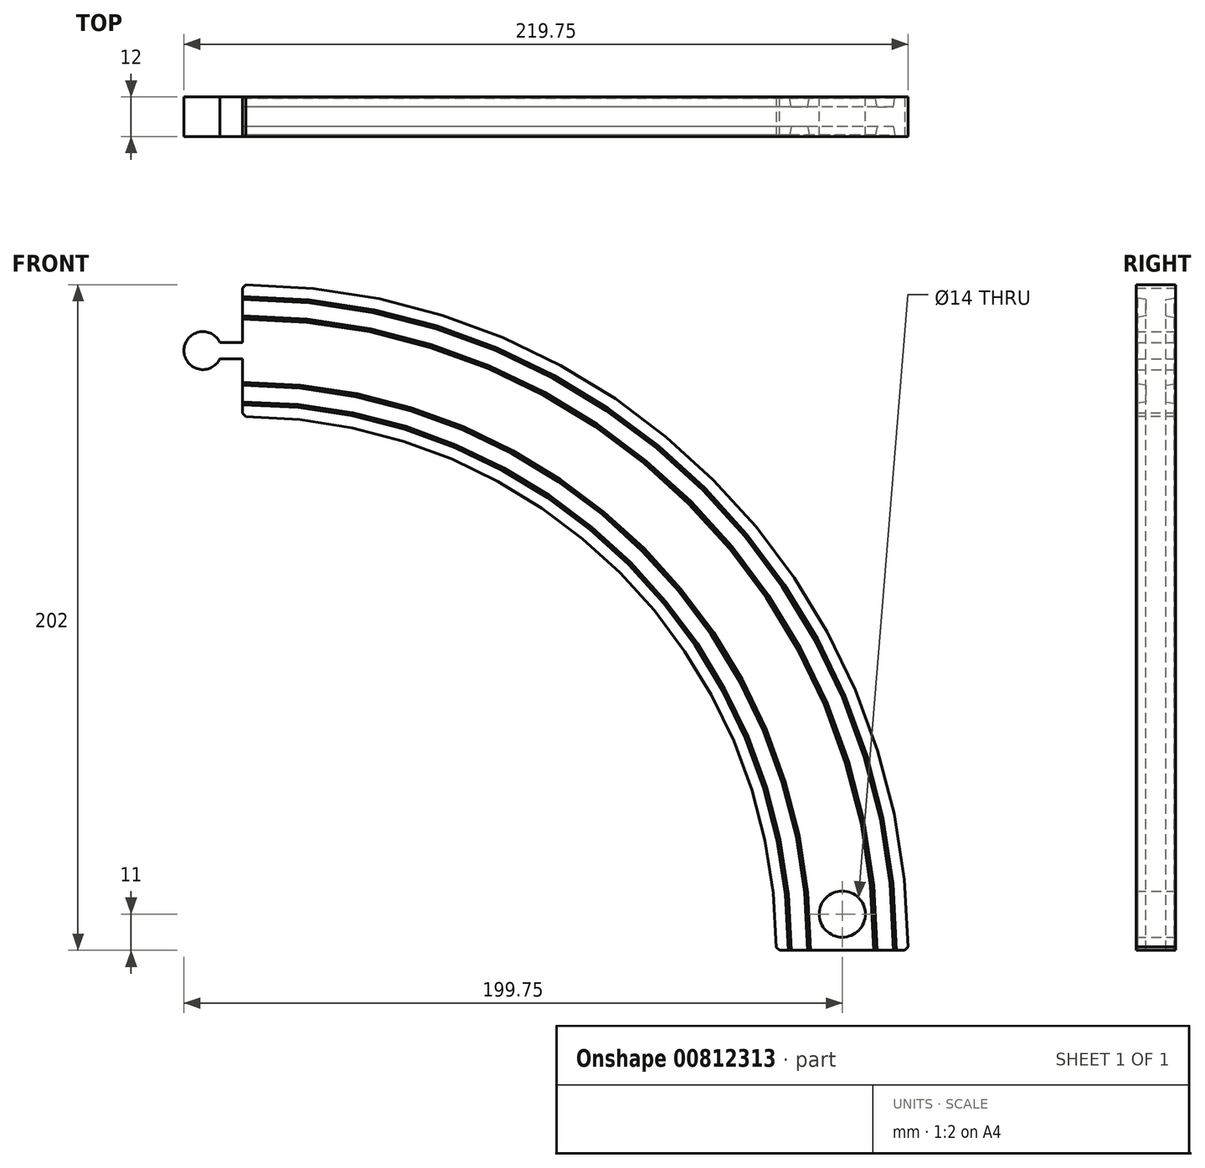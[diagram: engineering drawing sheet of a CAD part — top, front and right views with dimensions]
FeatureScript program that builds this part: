
annotation { "Feature Type Name" : "Feature", "Feature Type Description" : "" }
export const myFeature = defineFeature(function(context is Context, id is Id, definition is map)
    precondition{}
    {
        {
            var Q0;
            Q0=qCreatedBy(makeId("Top.planeOp"),FACE);
            var sketch = newSketch(context, id + "F0", { "sketchPlane" : qUnion([Q0])});
            skLineSegment(sketch, "E0.bottom", {"start": v(-20, 6) * mm, "end": v(20, 6) * mm});
            skLineSegment(sketch, "E0.top", {"start": v(-20, -6) * mm, "end": v(20, -6) * mm});
            skLineSegment(sketch, "E0.left", {"start": v(-20, 6) * mm, "end": v(-20, -6) * mm});
            skLineSegment(sketch, "E0.right", {"start": v(20, 6) * mm, "end": v(20, -6) * mm});
            skLineSegment(sketch, "E1", {"start": v(10.53, 3) * mm, "end": v(15.53, 3) * mm});
            skLineSegment(sketch, "E2", {"start": v(-15.53, 3) * mm, "end": v(-10.53, 3) * mm});
            skLineSegment(sketch, "E3", {"start": v(-20, 6) * mm, "end": v(20, -6) * mm, "construction": true});
            skLineSegment(sketch, "E4", {"start": v(-10.53, 3) * mm, "end": v(-10, 6) * mm});
            skLineSegment(sketch, "E5", {"start": v(-15.53, 3) * mm, "end": v(-16, 6) * mm});
            skLineSegment(sketch, "E6", {"start": v(10.53, 3) * mm, "end": v(10, 6) * mm});
            skLineSegment(sketch, "E7", {"start": v(15.53, 3) * mm, "end": v(16, 6) * mm});
            skLineSegment(sketch, "E8", {"start": v(15.53, -3) * mm, "end": v(10.53, -3) * mm});
            skLineSegment(sketch, "E9", {"start": v(15.53, -3) * mm, "end": v(16, -6) * mm});
            skLineSegment(sketch, "E10", {"start": v(10.53, -3) * mm, "end": v(10, -6) * mm});
            skLineSegment(sketch, "E11", {"start": v(-10.53, -3) * mm, "end": v(-15.53, -3) * mm});
            skLineSegment(sketch, "E12", {"start": v(-10.53, -3) * mm, "end": v(-10, -6) * mm});
            skLineSegment(sketch, "E13", {"start": v(-15.53, -3) * mm, "end": v(-16, -6) * mm});
            skLineSegment(sketch, "E14", {"start": v(10, 6) * mm, "end": v(10, -6) * mm, "construction": true});
            skLineSegment(sketch, "E15", {"start": v(16, 6) * mm, "end": v(16, -6) * mm, "construction": true});
            skLineSegment(sketch, "E16", {"start": v(10.53, 3) * mm, "end": v(10.53, -6) * mm, "construction": true});
            skLineSegment(sketch, "E17", {"start": v(-15.53, 3) * mm, "end": v(-15.53, -6) * mm, "construction": true});
            skSolve(sketch);
        }
        {
            var Q0;
            Q0=qCreatedBy(makeId("Front.planeOp"),FACE);
            var sketch = newSketch(context, id + "F1", { "sketchPlane" : qUnion([Q0])});
            skArc(sketch, "E18", {"start": v(0, 0) * mm, "mid": v(-53.3, 128.7) * mm, "end": v(-182, 182) * mm});
            skLineSegment(sketch, "E19", {"start": v(-182, 0) * mm, "end": v(-182, 247.89) * mm, "construction": true});
            skSolve(sketch);
        }
        {
            var Q0;
            Q0=makeQuery(id+"F0.imprint","IMPRINT",FACE,{"disambiguationData":[TD([[makeQuery(id+"F0.imprint","IMPRINT",EDGE,{"derivedFrom":sQuery(id+"F0.wireOp",EDGE,"E0.top")}),1.0]])]});
            var Q1;
            Q1=sQuery(id+"F1.wireOp",EDGE,"E18");
            sweep(context, id + "F2", {"profiles" : qUnion([Q0]), "path" : qUnion([Q1])});
        }
        {
            var Q0;
            Q0=makeQuery(id+"F2.opSweep","SWEPT_EDGE",EDGE,{"disambiguationData":[OSD([sQuery(id+"F0.wireOp",EDGE,"E0.bottom"),sQuery(id+"F0.wireOp",EDGE,"E4"),sQuery(id+"F1.wireOp",EDGE,"QheDVgyy-v1Xf-DTUT-CkoZ-R19I37jAeaWV")])]});
            var Q1;
            Q1=makeQuery(id+"F2.opSweep","SWEPT_EDGE",EDGE,{"disambiguationData":[OSD([sQuery(id+"F0.wireOp",EDGE,"E0.bottom"),sQuery(id+"F0.wireOp",EDGE,"E5"),sQuery(id+"F1.wireOp",EDGE,"QheDVgyy-v1Xf-DTUT-CkoZ-R19I37jAeaWV")])]});
            var Q2;
            Q2=makeQuery(id+"F2.opSweep","SWEPT_EDGE",EDGE,{"disambiguationData":[OSD([sQuery(id+"F0.wireOp",EDGE,"E0.bottom"),sQuery(id+"F0.wireOp",EDGE,"E6"),sQuery(id+"F1.wireOp",EDGE,"QheDVgyy-v1Xf-DTUT-CkoZ-R19I37jAeaWV")])]});
            var Q3;
            Q3=makeQuery(id+"F2.opSweep","SWEPT_EDGE",EDGE,{"disambiguationData":[OSD([sQuery(id+"F0.wireOp",EDGE,"E0.bottom"),sQuery(id+"F0.wireOp",EDGE,"E7"),sQuery(id+"F1.wireOp",EDGE,"QheDVgyy-v1Xf-DTUT-CkoZ-R19I37jAeaWV")])]});
            var Q4;
            Q4=makeQuery(id+"F2.opSweep","SWEPT_EDGE",EDGE,{"disambiguationData":[OSD([sQuery(id+"F0.wireOp",EDGE,"E0.top"),sQuery(id+"F0.wireOp",EDGE,"E10"),sQuery(id+"F1.wireOp",EDGE,"E18")])]});
            var Q5;
            Q5=makeQuery(id+"F2.opSweep","SWEPT_EDGE",EDGE,{"disambiguationData":[OSD([sQuery(id+"F0.wireOp",EDGE,"E0.top"),sQuery(id+"F0.wireOp",EDGE,"E9"),sQuery(id+"F1.wireOp",EDGE,"E18")])]});
            var Q6;
            Q6=makeQuery(id+"F2.opSweep","SWEPT_EDGE",EDGE,{"disambiguationData":[OSD([sQuery(id+"F0.wireOp",EDGE,"E0.top"),sQuery(id+"F0.wireOp",EDGE,"E13"),sQuery(id+"F1.wireOp",EDGE,"E18")])]});
            var Q7;
            Q7=makeQuery(id+"F2.opSweep","SWEPT_EDGE",EDGE,{"disambiguationData":[OSD([sQuery(id+"F0.wireOp",EDGE,"E0.top"),sQuery(id+"F0.wireOp",EDGE,"E12"),sQuery(id+"F1.wireOp",EDGE,"E18")])]});
            chamfer(context, id + "F3", {"entities" : qUnion([Q0, Q1, Q2, Q3, Q4, Q5, Q6, Q7]), "width" : 0.5 * mm, "tangentPropagation" : true});
        }
        {
            var Q0;
            Q0=qCreatedBy(makeId("Front.planeOp"),FACE);
            var sketch = newSketch(context, id + "F4", { "sketchPlane" : qUnion([Q0])});
            skLineSegment(sketch, "E20.0", {"start": v(-182, 191.5) * mm, "end": v(-182, 172.5) * mm});
            skSolve(sketch);
        }
        {
            var Q0;
            Q0=qCreatedBy(makeId("Front.planeOp"),FACE);
            var sketch = newSketch(context, id + "F5", { "sketchPlane" : qUnion([Q0])});
            skLineSegment(sketch, "E21.0", {"start": v(9.5, 0) * mm, "end": v(-9.5, 0) * mm});
            skLineSegment(sketch, "E22.bottom", {"start": v(3.5, 0) * mm, "end": v(-3.5, 0) * mm});
            skLineSegment(sketch, "E22.top", {"start": v(3.5, 5) * mm, "end": v(-3.5, 5) * mm});
            skLineSegment(sketch, "E22.left", {"start": v(3.5, 0) * mm, "end": v(3.5, 5) * mm});
            skLineSegment(sketch, "E22.right", {"start": v(-3.5, 0) * mm, "end": v(-3.5, 5) * mm});
            skLineSegment(sketch, "E23", {"start": v(9.5, 0) * mm, "end": v(3.5, 0) * mm, "construction": true});
            skLineSegment(sketch, "E24", {"start": v(-3.5, 0) * mm, "end": v(-9.5, 0) * mm, "construction": true});
            skCircle(sketch, "E25", {"center": v(0, 11) * mm, "radius": 7 * mm});
            skPoint(sketch, "E25.centerSnap0", {"position": v(0, 5) * mm});
            skSolve(sketch);
        }
        {
            var Q0;
            {var subQ0=sQuery(id+"F1.wireOp",EDGE,"QheDVgyy-v1Xf-DTUT-CkoZ-R19I37jAeaWV");var subQ1=sQuery(id+"F0.wireOp",EDGE,"E0.bottom");Q0=makeQuery(id+"F2.opSweep","SWEPT_FACE",FACE,{"disambiguationData":[OSD([subQ1,subQ0]),TDD([makeQuery(id+"F0.imprint","IMPRINT",EDGE,{"disambiguationData":[TD([[makeQuery(id+"F0.imprint","INTERSECT",VERTEX,{"derivedFrom":[subQ1,sQuery(id+"F0.wireOp",EDGE,"E4")]}),-1.0]])],"derivedFrom":subQ1}),subQ0])]});}
            var sketch = newSketch(context, id + "F6", { "sketchPlane" : qUnion([Q0])});
            skCircle(sketch, "E26.0", {"center": v(0, 11) * mm, "radius": 7 * mm});
            skLineSegment(sketch, "E27.0", {"start": v(3.5, 0) * mm, "end": v(3.5, 5) * mm});
            skLineSegment(sketch, "E28.0", {"start": v(-3.5, 0) * mm, "end": v(-3.5, 5) * mm});
            skLineSegment(sketch, "E29.0", {"start": v(-3.5, 5) * mm, "end": v(3.5, 5) * mm});
            skLineSegment(sketch, "E30.0", {"start": v(-9.5, 0) * mm, "end": v(9.5, 0) * mm});
            skSolve(sketch);
        }
        {
            var Q0;
            {var subQ5=sQuery(id+"F6.wireOp",EDGE,"E29.0");Q0=makeQuery(id+"F6.imprint","IMPRINT",FACE,{"disambiguationData":[TD([[makeQuery(id+"F6.imprint","IMPRINT",EDGE,{"derivedFrom":subQ5}),1.0]])]});}
            var Q1;
            {var subQ0=sQuery(id+"F6.wireOp",EDGE,"E27.0");var subQ1=sQuery(id+"F6.wireOp",EDGE,"E26.0");var subQ2=makeQuery(id+"F6.imprint","INTERSECT",VERTEX,{"derivedFrom":[subQ1,subQ0]});Q1=makeQuery(id+"F6.imprint","IMPRINT",FACE,{"disambiguationData":[TD([[makeQuery(id+"F6.imprint","IMPRINT",EDGE,{"disambiguationData":[TD([[subQ2,-1.0]])],"derivedFrom":subQ1}),1.0]])]});}
            var Q2;
            {var subQ5=sQuery(id+"F6.wireOp",EDGE,"E29.0");Q2=makeQuery(id+"F6.imprint","IMPRINT",FACE,{"disambiguationData":[TD([[makeQuery(id+"F6.imprint","IMPRINT",EDGE,{"derivedFrom":subQ5}),-1.0]])]});}
            extrude(context, id + "F7", {"entities" : qUnion([Q0, Q1, Q2]), "operationType" : NewBodyOperationType.REMOVE, "oppositeDirection" : true, "depth" : 25.4 * mm, "offsetDistance" : 25.4 * mm});
        }
        {
            var Q0;
            Q0=makeQuery(id+"F2.opSweep","CAP_EDGE",EDGE,{"disambiguationData":[OSD([sQuery(id+"F0.wireOp",EDGE,"E0.right"),sQuery(id+"F1.wireOp",VERTEX,"QheDVgyy-v1Xf-DTUT-CkoZ-R19I37jAeaWV.start")])],"isStart":false});
            var Q1;
            Q1=makeQuery(id+"F2.opSweep","CAP_EDGE",EDGE,{"disambiguationData":[OSD([sQuery(id+"F0.wireOp",EDGE,"E0.left"),sQuery(id+"F1.wireOp",VERTEX,"QheDVgyy-v1Xf-DTUT-CkoZ-R19I37jAeaWV.start")])],"isStart":false});
            var Q2;
            Q2=makeQuery(id+"F2.opSweep","CAP_EDGE",EDGE,{"disambiguationData":[OSD([sQuery(id+"F0.wireOp",EDGE,"E0.left"),sQuery(id+"F1.wireOp",VERTEX,"QheDVgyy-v1Xf-DTUT-CkoZ-R19I37jAeaWV.end")])],"isStart":true});
            var Q3;
            Q3=makeQuery(id+"F2.opSweep","CAP_EDGE",EDGE,{"disambiguationData":[OSD([sQuery(id+"F0.wireOp",EDGE,"E0.right"),sQuery(id+"F1.wireOp",VERTEX,"QheDVgyy-v1Xf-DTUT-CkoZ-R19I37jAeaWV.end")])],"isStart":true});
            chamfer(context, id + "F8", {"entities" : qUnion([Q0, Q1, Q2, Q3]), "width" : 1 * mm, "tangentPropagation" : true});
        }
        {
            var Q0;
            {var subQ0=sQuery(id+"F1.wireOp",EDGE,"E18");var subQ1=sQuery(id+"F0.wireOp",EDGE,"E0.bottom");Q0=makeQuery(id+"F2.opSweep","SWEPT_FACE",FACE,{"disambiguationData":[OSD([subQ1,subQ0]),TDD([makeQuery(id+"F0.imprint","IMPRINT",EDGE,{"disambiguationData":[TD([[makeQuery(id+"F0.imprint","INTERSECT",VERTEX,{"derivedFrom":[subQ1,sQuery(id+"F0.wireOp",EDGE,"E4")]}),-1.0]])],"derivedFrom":subQ1}),subQ0])]});}
            var sketch = newSketch(context, id + "F9", { "sketchPlane" : qUnion([Q0])});
            skLineSegment(sketch, "E31.0", {"start": v(182, 191.5) * mm, "end": v(182, 172.5) * mm});
            skLineSegment(sketch, "E32", {"start": v(182, 179.5) * mm, "end": v(189, 179.5) * mm});
            skLineSegment(sketch, "E33", {"start": v(189, 179.5) * mm, "end": v(189, 184.5) * mm});
            skLineSegment(sketch, "E34", {"start": v(189, 184.5) * mm, "end": v(182, 184.5) * mm});
            skLineSegment(sketch, "E35", {"start": v(182, 184.5) * mm, "end": v(182, 191.5) * mm, "construction": true});
            skLineSegment(sketch, "E36", {"start": v(182, 172.5) * mm, "end": v(182, 179.5) * mm, "construction": true});
            skCircle(sketch, "E37", {"center": v(194, 182) * mm, "radius": 5.75 * mm});
            skPoint(sketch, "E37.centerSnap0", {"position": v(189, 182) * mm});
            skSolve(sketch);
        }
        {
            var Q0;
            {var subQ0=sQuery(id+"F9.wireOp",EDGE,"E33");Q0=makeQuery(id+"F9.imprint","IMPRINT",FACE,{"disambiguationData":[TD([[makeQuery(id+"F9.imprint","IMPRINT",EDGE,{"derivedFrom":subQ0}),-1.0]])]});}
            var Q1;
            {var subQ0=sQuery(id+"F9.wireOp",EDGE,"E33");Q1=makeQuery(id+"F9.imprint","IMPRINT",FACE,{"disambiguationData":[TD([[makeQuery(id+"F9.imprint","IMPRINT",EDGE,{"derivedFrom":subQ0}),1.0]])]});}
            var Q2;
            {var subQ0=sQuery(id+"F9.wireOp",EDGE,"E32");var subQ1=sQuery(id+"F9.wireOp",EDGE,"E31.0");var subQ2=makeQuery(id+"F9.imprint","INTERSECT",VERTEX,{"derivedFrom":[subQ1,subQ0]});Q2=makeQuery(id+"F9.imprint","IMPRINT",FACE,{"disambiguationData":[TD([[makeQuery(id+"F9.imprint","IMPRINT",EDGE,{"disambiguationData":[TD([[subQ2,1.0]])],"derivedFrom":subQ1}),1.0]])]});}
            extrude(context, id + "F10", {"entities" : qUnion([Q0, Q1, Q2]), "operationType" : NewBodyOperationType.ADD, "oppositeDirection" : true, "depth" : 12 * mm, "offsetDistance" : 25.4 * mm});
        }
    });
